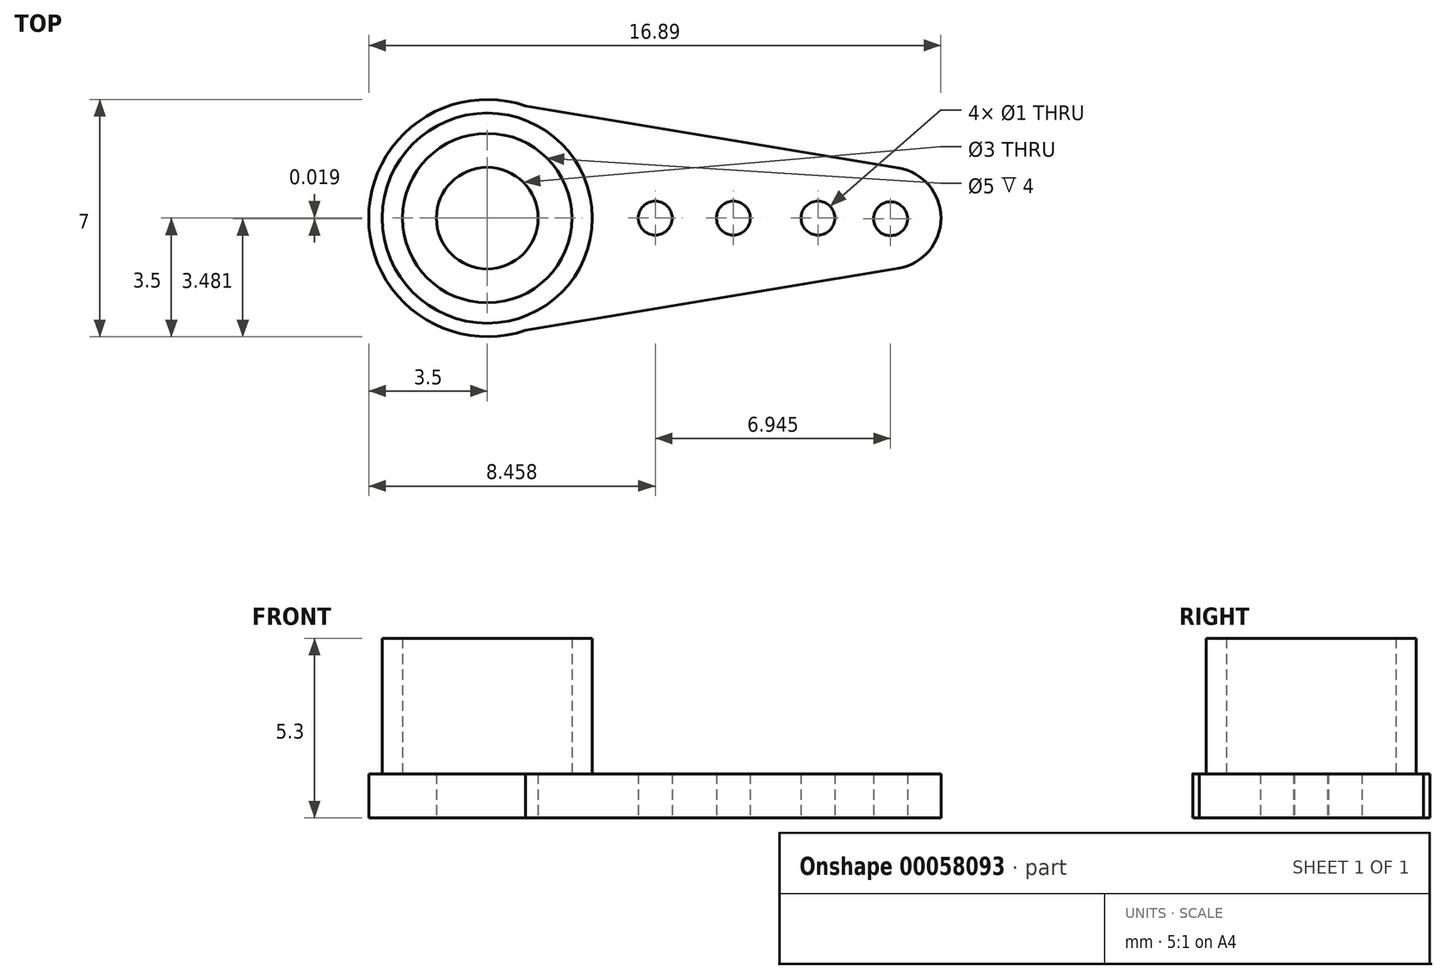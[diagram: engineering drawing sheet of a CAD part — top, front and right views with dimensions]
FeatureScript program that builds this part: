
annotation { "Feature Type Name" : "Feature", "Feature Type Description" : "" }
export const myFeature = defineFeature(function(context is Context, id is Id, definition is map)
    precondition{}
    {
        {
            var Q0;
            Q0=qCreatedBy(makeId("Top.planeOp"),FACE);
            var sketch = newSketch(context, id + "F0", { "sketchPlane" : qUnion([Q0])});
            skCircle(sketch, "E0", {"center": v(0, 0) * mm, "radius": 1.5 * mm});
            skArc(sketch, "E1", {"start": v(1.13, 3.31) * mm, "mid": v(-3.5, 0) * mm, "end": v(1.13, -3.31) * mm});
            skArc(sketch, "E2", {"start": v(12.14, -1.48) * mm, "mid": v(13.4, 0) * mm, "end": v(12.14, 1.48) * mm});
            skLineSegment(sketch, "E3", {"start": v(0, 3.5) * mm, "end": v(12.14, 1.48) * mm});
            skLineSegment(sketch, "E4", {"start": v(0, -3.5) * mm, "end": v(12.14, -1.48) * mm});
            skCircle(sketch, "E5", {"center": v(4.96, 0) * mm, "radius": 0.5 * mm});
            skCircle(sketch, "E6", {"center": v(7.26, 0) * mm, "radius": 0.5 * mm});
            skCircle(sketch, "E7", {"center": v(9.76, 0) * mm, "radius": 0.5 * mm});
            skCircle(sketch, "E8", {"center": v(11.9, -0.02) * mm, "radius": 0.5 * mm});
            skSolve(sketch);
        }
        {
            var Q0;
            Q0 = qSketchRegion(id + "F0", true);
            var Q1;
            Q1=makeQuery(id+"F0.imprint","IMPRINT",FACE,{"disambiguationData":[TD([[makeQuery(id+"F0.imprint","IMPRINT",EDGE,{"derivedFrom":sQuery(id+"F0.wireOp",EDGE,"E0")}),-1.0]])]});
            extrude(context, id + "F1", {"entities" : qUnion([Q0, Q1]), "depth" : 1.3 * mm});
        }
        {
            var Q0;
            Q0=makeQuery(id+"F1.opExtrude","CAP_FACE",FACE,{"disambiguationData":[OSD([sQuery(id+"F0.wireOp",EDGE,"E0"),sQuery(id+"F0.wireOp",EDGE,"E1"),sQuery(id+"F0.wireOp",EDGE,"E2"),sQuery(id+"F0.wireOp",EDGE,"E3"),sQuery(id+"F0.wireOp",EDGE,"E4"),sQuery(id+"F0.wireOp",EDGE,"E5"),sQuery(id+"F0.wireOp",EDGE,"E6"),sQuery(id+"F0.wireOp",EDGE,"E7"),sQuery(id+"F0.wireOp",EDGE,"E8")])],"isStart":false});
            var sketch = newSketch(context, id + "F2", { "sketchPlane" : qUnion([Q0])});
            skCircle(sketch, "E9", {"center": v(0, 0) * mm, "radius": 2.5 * mm});
            skCircle(sketch, "E10", {"center": v(0, 0) * mm, "radius": 3.1 * mm});
            skSolve(sketch);
        }
        {
            var Q0;
            Q0=makeQuery(id+"F2.imprint","IMPRINT",FACE,{"disambiguationData":[TD([[makeQuery(id+"F2.imprint","IMPRINT",EDGE,{"derivedFrom":sQuery(id+"F2.wireOp",EDGE,"E9")}),-1.0]])]});
            extrude(context, id + "F3", {"entities" : qUnion([Q0]), "operationType" : NewBodyOperationType.ADD, "depth" : 4 * mm});
        }
    });
